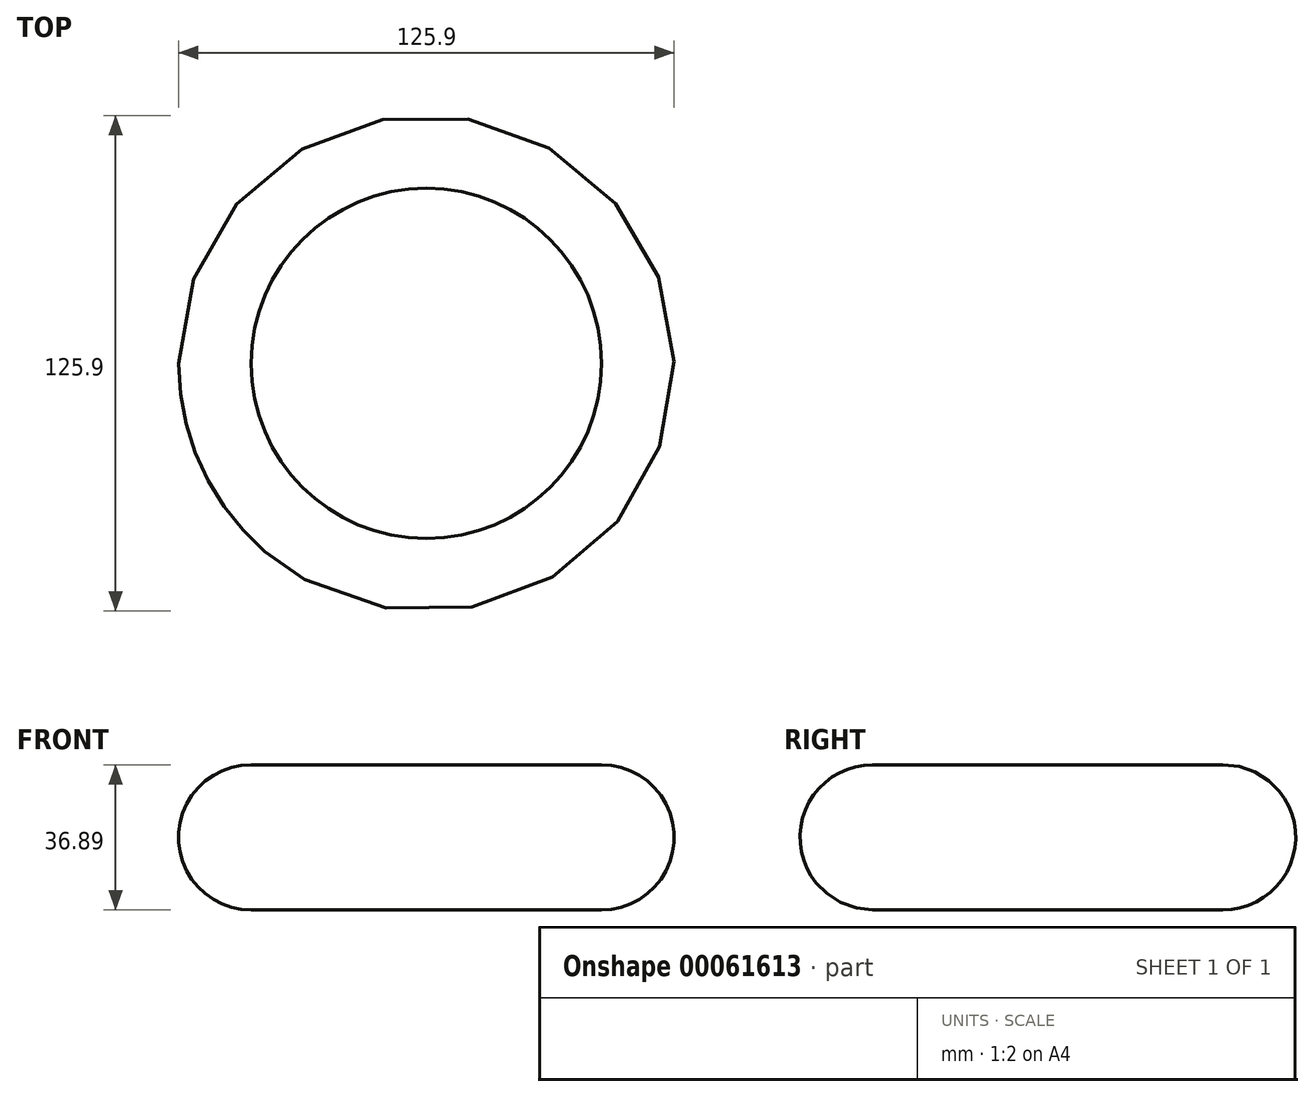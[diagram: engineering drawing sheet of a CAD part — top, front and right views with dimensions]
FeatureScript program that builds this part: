
annotation { "Feature Type Name" : "Feature", "Feature Type Description" : "" }
export const myFeature = defineFeature(function(context is Context, id is Id, definition is map)
    precondition{}
    {
        {
            var Q0;
            Q0=qCreatedBy(makeId("Front.planeOp"),FACE);
            var sketch = newSketch(context, id + "F0", { "sketchPlane" : qUnion([Q0])});
            skLineSegment(sketch, "E0", {"start": v(0, 0) * mm, "end": v(-44.51, 0) * mm});
            skLineSegment(sketch, "E1", {"start": v(0, 25.14) * mm, "end": v(0, -23.72) * mm});
            skArc(sketch, "E2", {"start": v(-44.51, 0) * mm, "mid": v(-62.95, 18.44) * mm, "end": v(-44.51, 36.89) * mm});
            skSolve(sketch);
        }
        {
            var Q0;
            Q0 = qSketchRegion(id + "F0", true);
            var Q1;
            Q1=sQuery(id+"F0.wireOp",EDGE,"E2");
            var Q2;
            Q2=sQuery(id+"F0.wireOp",EDGE,"E0");
            var Q3;
            Q3=sQuery(id+"F0.wireOp",EDGE,"E1");
            revolve(context, id + "F1", {"bodyType" : ToolBodyType.SURFACE, "entities" : qUnion([Q0]), "surfaceEntities" : qUnion([Q1, Q2]), "axis" : qUnion([Q3]), "revolveType" : RevolveType.FULL});
        }
    });
